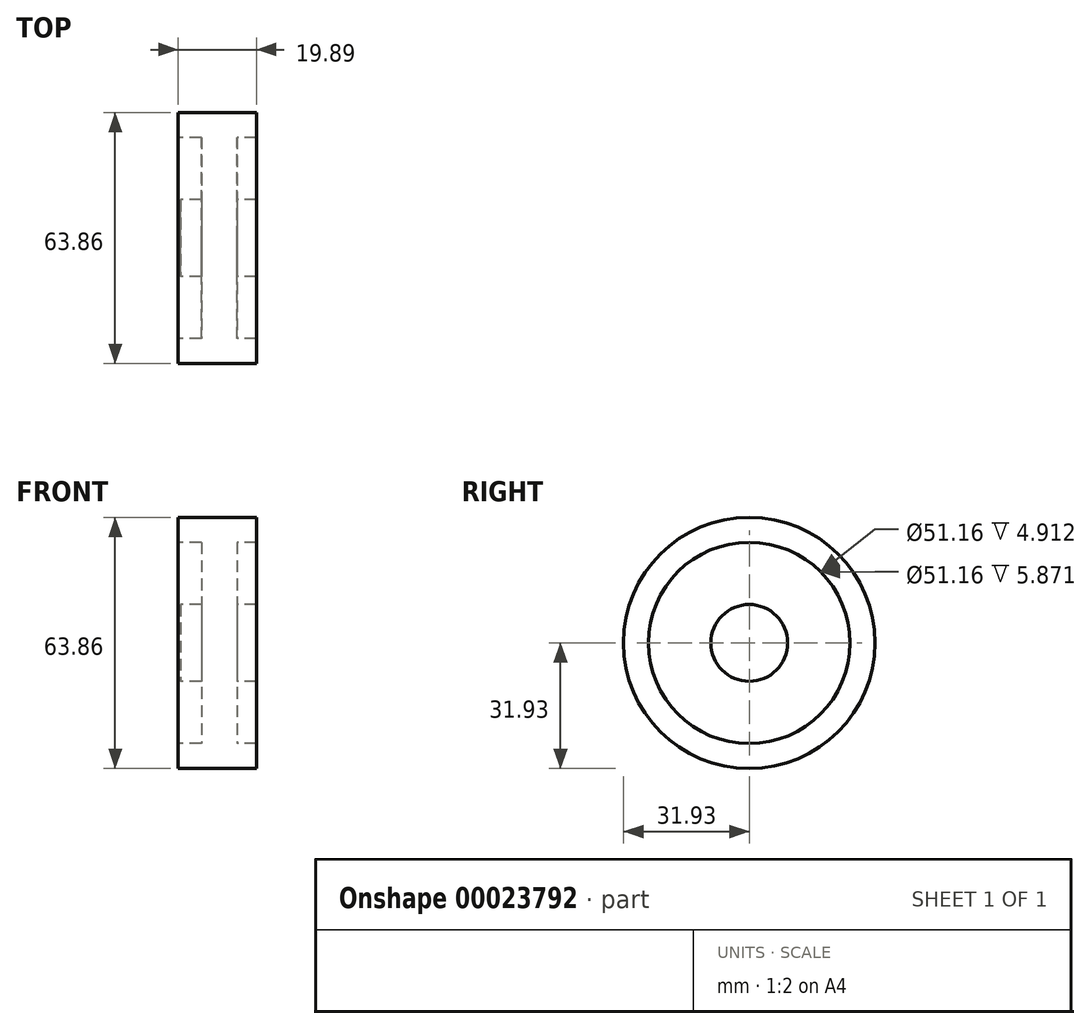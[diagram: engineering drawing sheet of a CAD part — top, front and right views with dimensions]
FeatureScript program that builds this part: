
annotation { "Feature Type Name" : "Feature", "Feature Type Description" : "" }
export const myFeature = defineFeature(function(context is Context, id is Id, definition is map)
    precondition{}
    {
        {
            var Q0;
            Q0=qCreatedBy(makeId("Front.planeOp"),FACE);
            var sketch = newSketch(context, id + "F0", { "sketchPlane" : qUnion([Q0])});
            skLineSegment(sketch, "E0", {"start": v(0, 0) * mm, "end": v(-68.41, 0) * mm, "construction": true});
            skLineSegment(sketch, "E1.bottom", {"start": v(-8.5, 9.76) * mm, "end": v(10.78, 9.76) * mm});
            skLineSegment(sketch, "E1.top", {"start": v(-8.5, 0) * mm, "end": v(10.78, 0) * mm});
            skLineSegment(sketch, "E1.left", {"start": v(-8.5, 9.76) * mm, "end": v(-8.5, 0) * mm});
            skLineSegment(sketch, "E1.right", {"start": v(10.78, 9.76) * mm, "end": v(10.78, 0) * mm});
            skLineSegment(sketch, "E2.bottom", {"start": v(-3.23, 9.76) * mm, "end": v(5.87, 9.76) * mm});
            skLineSegment(sketch, "E2.top", {"start": v(-3.23, 25.58) * mm, "end": v(5.87, 25.58) * mm});
            skLineSegment(sketch, "E2.left", {"start": v(-3.23, 9.76) * mm, "end": v(-3.23, 25.58) * mm});
            skLineSegment(sketch, "E2.right", {"start": v(5.87, 9.76) * mm, "end": v(5.87, 25.58) * mm});
            skLineSegment(sketch, "E3.bottom", {"start": v(-9.1, 25.58) * mm, "end": v(10.78, 25.58) * mm});
            skLineSegment(sketch, "E3.top", {"start": v(-9.1, 31.93) * mm, "end": v(10.78, 31.93) * mm});
            skLineSegment(sketch, "E3.left", {"start": v(-9.1, 25.58) * mm, "end": v(-9.1, 31.93) * mm});
            skLineSegment(sketch, "E3.right", {"start": v(10.78, 25.58) * mm, "end": v(10.78, 31.93) * mm});
            skSolve(sketch);
        }
        {
            var Q0;
            Q0 = qSketchRegion(id + "F0", true);
            var Q1;
            Q1=sQuery(id+"F0.wireOp",EDGE,"E1.top");
            revolve(context, id + "F1", {"entities" : qUnion([Q0]), "axis" : qUnion([Q1]), "revolveType" : RevolveType.FULL});
        }
    });
